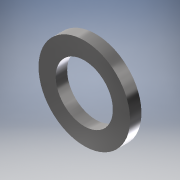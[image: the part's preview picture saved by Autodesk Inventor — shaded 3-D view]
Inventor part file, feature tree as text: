
AUTODESK INVENTOR PART (.ipt)
format: ipt  version: 2018 (Build 220112000, 112)  size: 104,960 bytes
history: native  units: mm
features: extrude x1, sketch x1
ambient origin geometry x8: Origin, YZ Plane, XZ Plane, XY Plane, X Axis, Y Axis, Z Axis, Center Point
bodies: Solid1 (feature_tree)
feature tree (2):
  extrude  "Extrusion1"  Depth=4.0mm
  sketch  "Sketch1"  dims[d0=20.0mm d1=32.0mm d2=4.0mm d3=0.0mm]
